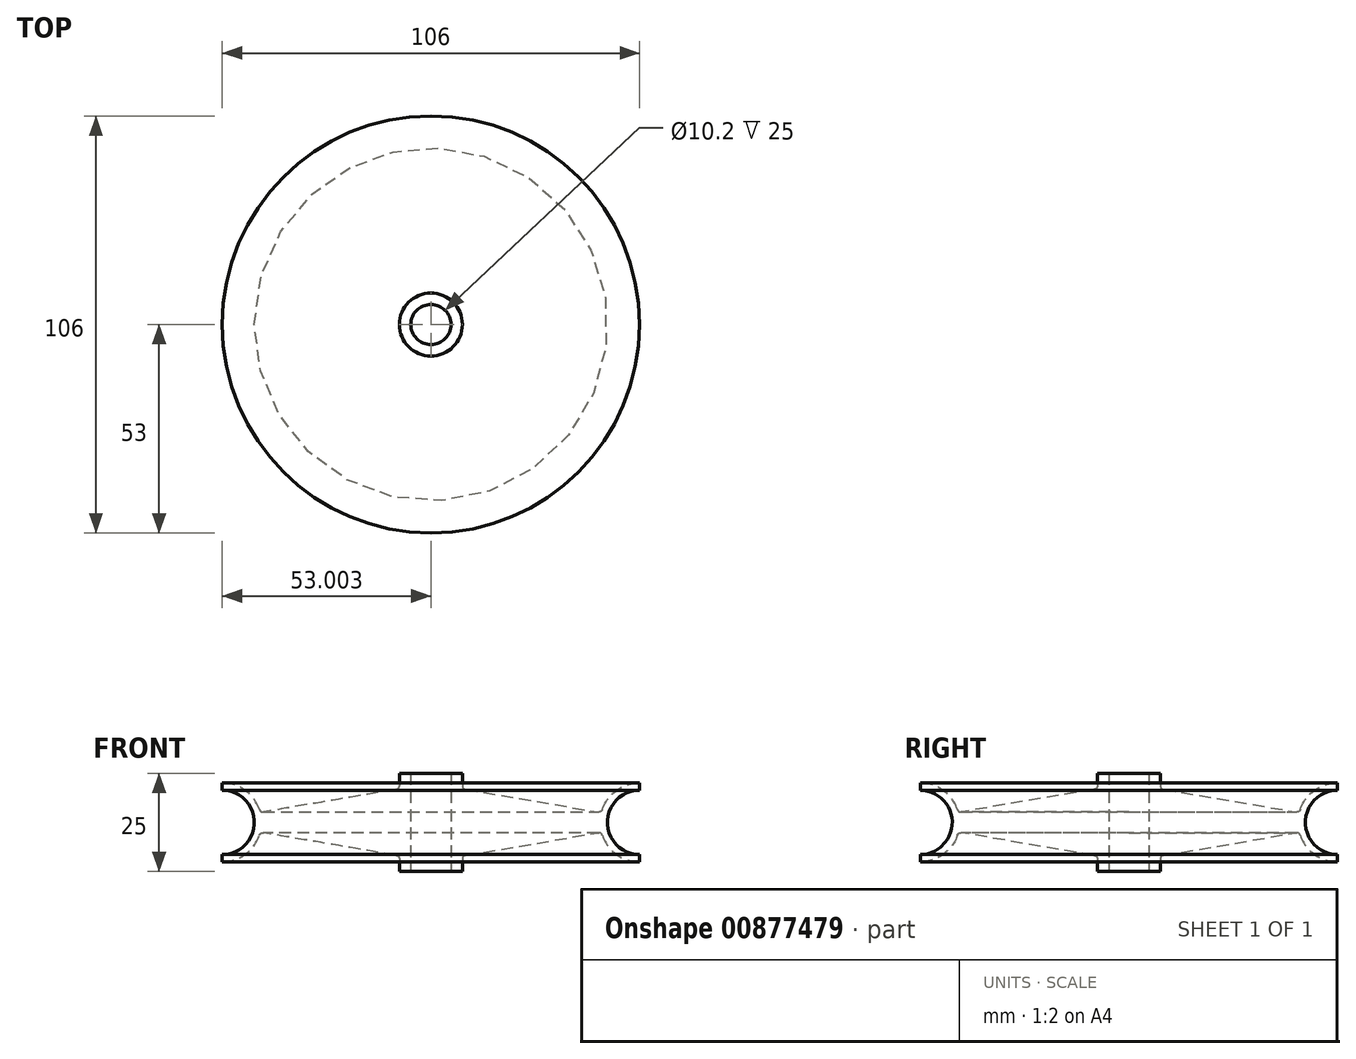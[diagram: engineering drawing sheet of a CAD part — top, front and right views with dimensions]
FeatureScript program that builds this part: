
annotation { "Feature Type Name" : "Feature", "Feature Type Description" : "" }
export const myFeature = defineFeature(function(context is Context, id is Id, definition is map)
    precondition{}
    {
        {
            var Q0;
            Q0=qCreatedBy(makeId("Front.planeOp"),FACE);
            var sketch = newSketch(context, id + "F0", { "sketchPlane" : qUnion([Q0])});
            skArc(sketch, "E0", {"start": v(-52.23, -0.58) * mm, "mid": v(-46.1, 1.52) * mm, "end": v(-42.54, 6.92) * mm});
            skArc(sketch, "E1", {"start": v(-52.23, 1.27) * mm, "mid": v(-44.08, 9.42) * mm, "end": v(-52.23, 17.57) * mm});
            skPoint(sketch, "E2", {"position": v(-52.23, 17.57) * mm});
            skPoint(sketch, "E3", {"position": v(-52.23, 19.42) * mm});
            skPoint(sketch, "E4", {"position": v(-52.23, 1.27) * mm});
            skPoint(sketch, "E5", {"position": v(-52.23, -0.58) * mm});
            skLineSegment(sketch, "E6", {"start": v(-52.23, 19.42) * mm, "end": v(-52.23, 17.57) * mm});
            skLineSegment(sketch, "E7", {"start": v(-52.23, 1.27) * mm, "end": v(-52.23, -0.58) * mm});
            skLineSegment(sketch, "E8.bottom", {"start": v(-7.23, 21.92) * mm, "end": v(-4.33, 21.92) * mm});
            skLineSegment(sketch, "E8.top", {"start": v(-7.23, -3.08) * mm, "end": v(-4.33, -3.08) * mm});
            skLineSegment(sketch, "E8.left", {"start": v(-7.23, 21.92) * mm, "end": v(-7.23, 17.92) * mm});
            skPoint(sketch, "E8.middle", {"position": v(0.77, 9.42) * mm});
            skLineSegment(sketch, "E9.right", {"start": v(-4.33, 21.92) * mm, "end": v(-4.33, -3.08) * mm});
            skPoint(sketch, "E10", {"position": v(-4.33, 21.92) * mm});
            skPoint(sketch, "E11", {"position": v(5.87, 21.92) * mm});
            skPoint(sketch, "E12", {"position": v(5.87, -3.08) * mm});
            skPoint(sketch, "E13", {"position": v(-4.33, -3.08) * mm});
            skPoint(sketch, "E14", {"position": v(-42.54, 11.92) * mm});
            skPoint(sketch, "E15", {"position": v(-7.23, 17.92) * mm});
            skLineSegment(sketch, "E16", {"start": v(-42.54, 11.92) * mm, "end": v(-7.23, 17.92) * mm});
            skPoint(sketch, "E17", {"position": v(-42.23, 9.42) * mm});
            skLineSegment(sketch, "E18.MirrorCS", {"start": v(-42.54, 6.92) * mm, "end": v(-7.23, 0.92) * mm});
            skArc(sketch, "E19.trimOffspring", {"start": v(-42.54, 11.92) * mm, "mid": v(-46.1, 17.33) * mm, "end": v(-52.23, 19.42) * mm});
            skPoint(sketch, "E20.orphan", {"position": v(0.77, -3.08) * mm});
            skPoint(sketch, "E21.end.orphan", {"position": v(0.77, 21.92) * mm});
            skPoint(sketch, "E22.orphan", {"position": v(8.77, 21.92) * mm});
            skPoint(sketch, "E23.trimOffspring.end.orphan", {"position": v(8.77, -3.08) * mm});
            skLineSegment(sketch, "E24.trimOffspring", {"start": v(-7.23, 0.92) * mm, "end": v(-7.23, -3.08) * mm});
            skLineSegment(sketch, "E25", {"start": v(0.77, -33.53) * mm, "end": v(0.77, 54.93) * mm});
            skSolve(sketch);
        }
        {
            var Q0;
            Q0=makeQuery(id+"F0.imprint","IMPRINT",FACE,{"disambiguationData":[TD([[makeQuery(id+"F0.imprint","IMPRINT",EDGE,{"derivedFrom":sQuery(id+"F0.wireOp",EDGE,"E0")}),1.0]])]});
            var Q1;
            Q1=sQuery(id+"F0.wireOp",EDGE,"E25");
            revolve(context, id + "F1", {"surfaceOperationType" : NewSurfaceOperationType.NEW, "entities" : qUnion([Q0]), "axis" : qUnion([Q1]), "revolveType" : RevolveType.FULL});
        }
        {
            var Q0;
            Q0=makeQuery(id+"F1.opRevolve","SWEPT_EDGE",EDGE,{"disambiguationData":[OSD([sQuery(id+"F0.wireOp",EDGE,"E0"),sQuery(id+"F0.wireOp",EDGE,"E18.MirrorCS")])]});
            var Q1;
            Q1=makeQuery(id+"F1.opRevolve","SWEPT_EDGE",EDGE,{"disambiguationData":[OSD([sQuery(id+"F0.wireOp",EDGE,"E16"),sQuery(id+"F0.wireOp",EDGE,"E19.trimOffspring")])]});
            var Q2;
            Q2=makeQuery(id+"F1.opRevolve","SWEPT_EDGE",EDGE,{"disambiguationData":[OSD([sQuery(id+"F0.wireOp",EDGE,"E18.MirrorCS"),sQuery(id+"F0.wireOp",EDGE,"E24.trimOffspring")])]});
            var Q3;
            Q3=makeQuery(id+"F1.opRevolve","SWEPT_EDGE",EDGE,{"disambiguationData":[OSD([sQuery(id+"F0.wireOp",EDGE,"E8.left"),sQuery(id+"F0.wireOp",EDGE,"E16")])]});
            fillet(context, id + "F2", {"entities" : qUnion([Q0, Q1, Q2, Q3]), "radius" : 1 * mm, "tangentPropagation" : true, "rho" : 0.5, "crossSection" : FilletCrossSection.CONIC, "allowEdgeOverflow" : false});
        }
    });
